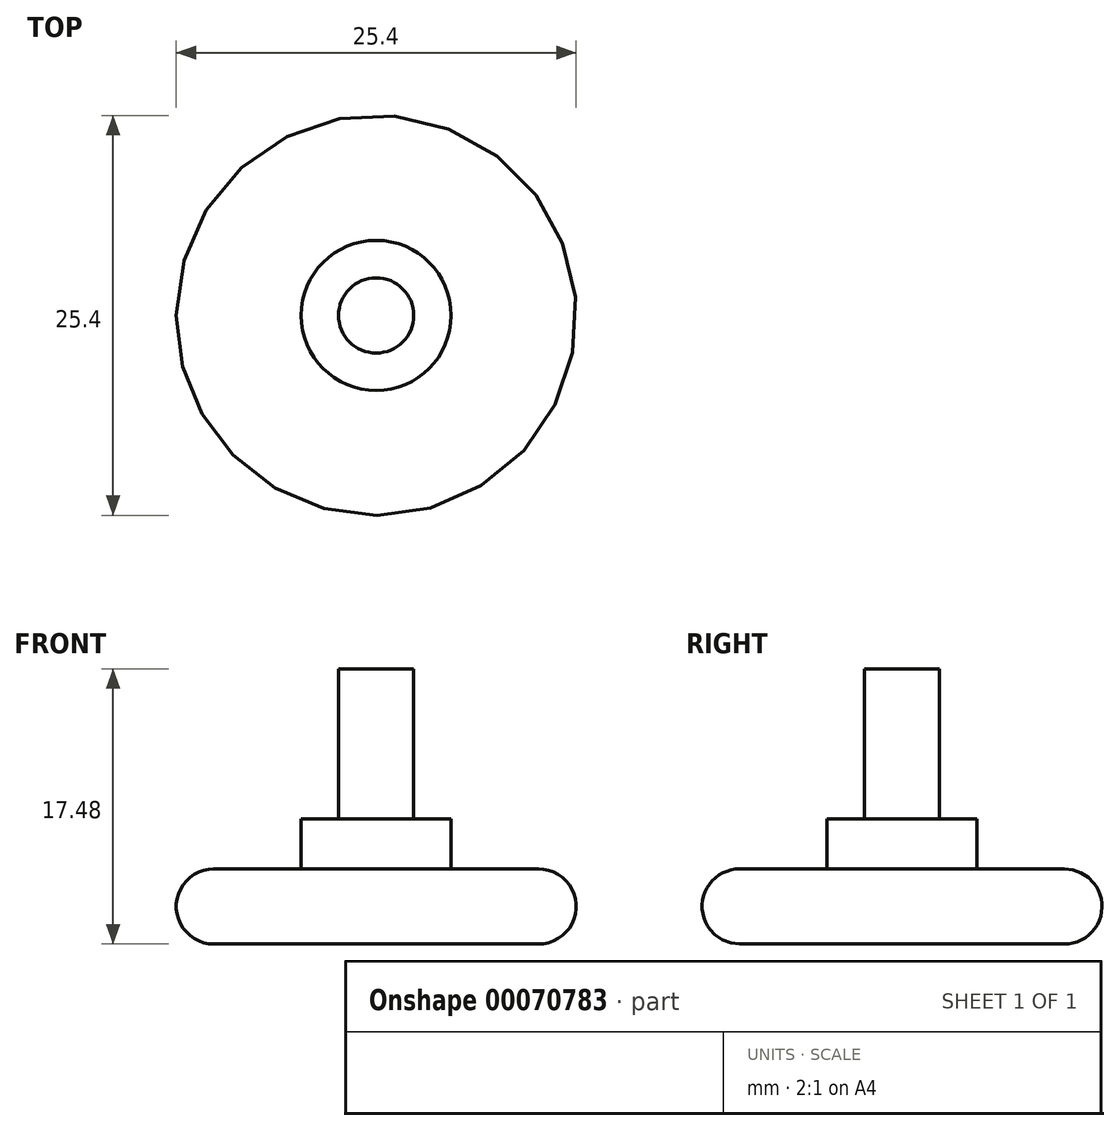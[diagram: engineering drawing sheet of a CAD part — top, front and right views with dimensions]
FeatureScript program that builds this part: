
annotation { "Feature Type Name" : "Feature", "Feature Type Description" : "" }
export const myFeature = defineFeature(function(context is Context, id is Id, definition is map)
    precondition{}
    {
        {
            var Q0;
            Q0=qCreatedBy(makeId("Front.planeOp"),FACE);
            var sketch = newSketch(context, id + "F0", { "sketchPlane" : qUnion([Q0])});
            skLineSegment(sketch, "E0.bottom", {"start": v(0, 0) * mm, "end": v(12.7, 0) * mm});
            skLineSegment(sketch, "E0.top", {"start": v(0, 4.78) * mm, "end": v(12.7, 4.78) * mm});
            skLineSegment(sketch, "E0.left", {"start": v(0, 0) * mm, "end": v(0, 4.78) * mm});
            skLineSegment(sketch, "E0.right", {"start": v(12.7, 0) * mm, "end": v(12.7, 4.78) * mm});
            skSolve(sketch);
        }
        {
            var Q0;
            Q0 = qSketchRegion(id + "F0", true);
            var Q1;
            Q1=sQuery(id+"F0.wireOp",EDGE,"E0.left");
            revolve(context, id + "F1", {"entities" : qUnion([Q0]), "axis" : qUnion([Q1]), "revolveType" : RevolveType.FULL});
        }
        {
            var Q0;
            Q0=makeQuery(id+"F1.opRevolve","SWEPT_EDGE",EDGE,{"disambiguationData":[OSD([sQuery(id+"F0.wireOp",EDGE,"E0.top"),sQuery(id+"F0.wireOp",EDGE,"E0.right")])]});
            var Q1;
            Q1=makeQuery(id+"F1.opRevolve","SWEPT_EDGE",EDGE,{"disambiguationData":[OSD([sQuery(id+"F0.wireOp",EDGE,"E0.bottom"),sQuery(id+"F0.wireOp",EDGE,"E0.right")])]});
            fillet(context, id + "F2", {"entities" : qUnion([Q0, Q1]), "radius" : 2.4 * mm, "tangentPropagation" : true, "allowEdgeOverflow" : false});
        }
        {
            var Q0;
            Q0=makeQuery(id+"F1.opRevolve","SWEPT_FACE",FACE,{"disambiguationData":[OSD([sQuery(id+"F0.wireOp",EDGE,"E0.top")])]});
            var sketch = newSketch(context, id + "F3", { "sketchPlane" : qUnion([Q0])});
            skCircle(sketch, "E1", {"center": v(0, 0) * mm, "radius": 4.76 * mm});
            skSolve(sketch);
        }
        {
            var Q0;
            Q0 = qSketchRegion(id + "F3", true);
            extrude(context, id + "F4", {"entities" : qUnion([Q0]), "operationType" : NewBodyOperationType.ADD, "depth" : 3.17 * mm});
        }
        {
            var Q0;
            Q0=makeQuery(id+"F4.opExtrude","CAP_FACE",FACE,{"disambiguationData":[OSD([sQuery(id+"F3.wireOp",EDGE,"E1")])],"isStart":false});
            var sketch = newSketch(context, id + "F5", { "sketchPlane" : qUnion([Q0])});
            skCircle(sketch, "E2", {"center": v(0, 0) * mm, "radius": 2.39 * mm});
            skSolve(sketch);
        }
        {
            var Q0;
            Q0 = qSketchRegion(id + "F5", true);
            extrude(context, id + "F6", {"entities" : qUnion([Q0]), "operationType" : NewBodyOperationType.ADD, "depth" : 9.52 * mm});
        }
    });
